# Revit family: Genelec_4040
name_source: partatom
category: Generic Models
units: mm (PartAtom-declared; Revit-internal decimal feet)

## family parameters
Always vertical = No
Can host rebar = No
Cut with Voids When Loaded = No
Maintain Annotation Orientation = No
Part Type = Normal
Room Calculation Point = Yes
Round Connector Dimension = Use Diameter
Shared = No
Work Plane-Based = No

## types (2) — shared parameters
Accuracy of Frequency Response = ± 3 dB (55 Hz - 20 kHz)
Acoustic Axis = 225
BIMobject category = Audio Electronics
Color = RAL_9018_Papyrus White
Default Elevation = 1200 mm
Depth = 223 mm  [stored 0.731627 ft]
Description = The 4040A Active Installation Loudspeaker is the largest of the 4000 series models, designed for larger installations that demand higher playback levels and greater low frequency extension.
Dispersion Angle = H 120° V 100°
Driver Dimensions = ⌀ 165 mm Woofer + ⌀ 19 mm Tweeter
Export Type to IFC As = IfcAudioVisualApplianceType
Finish Type = Die cast aluminium
Group Delay = 2.2 ms
Height = 350 mm  [stored 1.14829 ft]
IFC Classification = Electric Appliance
IFC Name = 4040A
Line Drawing = https://assets.ctfassets.net
Mains Voltage = 100, 120, 220 or 230VAC 50/60Hz according to region
Manufacturer = GENELEC
Manufacturer Country = Finland
Max. short term sine wave acoustic output  on axis in half space, averaged from 100Hz to 3 kHz = ≥ 109 dB SPL
Maximum long term RMS acoustic output in same conditions with IEC weighted noise (limited by driver unit protection circuit) = ≥ 101 dB SPL
Model = 4040A
Model Description = Active Installation Speaker
Model Image = https://images.ctfassets.net
Model Name = 4040A
Mounting Type = Includes mount: 4000-414B/W
Power Consumption = 170 W
Power consumption Idle = ≤15 W
Power consumption Standby = ≤0.5 W (ISS Active)
Product Family = Installation Speaker
Product Group = 4000 Series Installation Speakers
Self-generated Noise = ≤10 dB
Type IFC Predefined Type = SPEAKER
Type Image = <None>
URL = https://www.genelec.com
Uniclass 2.0 Description = Sound Amplifiers
Weight = 9.9
Width = 237 mm  [stored 0.777559 ft]

## per-type parameters (varying)
| type | Connections | Frequency Response | Horizontal Visibility | Price List Description | Vertical Visibility |
| 4040 Horizontal | 1 x Euroblock Analog Input

1 x RJ45 AES67 / Dante Input | 50 Hz - 25 kHz (-6 dB)
50 Hz - 25 kHz (-6 dB) | Yes | Recycled-aluminium cabinet with tightly controlled directivity and minimum diffraction for excellent performance. Both drivers have metal protection grilles, with 165 mm (6.5 in) LF and 19 mm (3/4 in) HF transducers. Integrated crossover and Class D amplifiers 120 W + 120 W. Max. SPL 109 dB, frequency response 50 Hz - 25 kHz (- 6 dB). Room response controls on rear panel to compensate the placement and room effects. On-Off switch on the rear panel. Autostart capable, 12 V remote power on/off switching.  Dimensions: H 350 x W 237 x D 223 mm, weight 9,9 kg. | No |
| 4040 Vertical | 1 x Euroblock Analog Input | 50 Hz - 25 kHz (-6 dB) | No | Recycled-aluminium cabinet with tightly controlled directivity and minimum diffraction for excellent performance. Both drivers have metal protection grilles, with 165 mm (6.5 in) LF and 19 mm (3/4 in) HF transducers. Integrated crossover and Class D amplifiers 120 W + 120 W. Max. SPL 109 dB, frequency response 50 Hz - 25 kHz (- 6 dB). Room response controls on rear panel to compensate the placement and room effects. On- Off switch on the rear panel. Autostart capable, 12 V remote power on/off switching. Dimensions: H 350 x W 237 x D 223 mm, weight 9,9 kg. | Yes |

note: [stored X ft] marks values corroborated as IEEE doubles in the binary element streams (Revit-internal decimal feet)

## geometry (parser evidence)
native form markers: Sweep x8
no freeform markers — native parametric forms only
